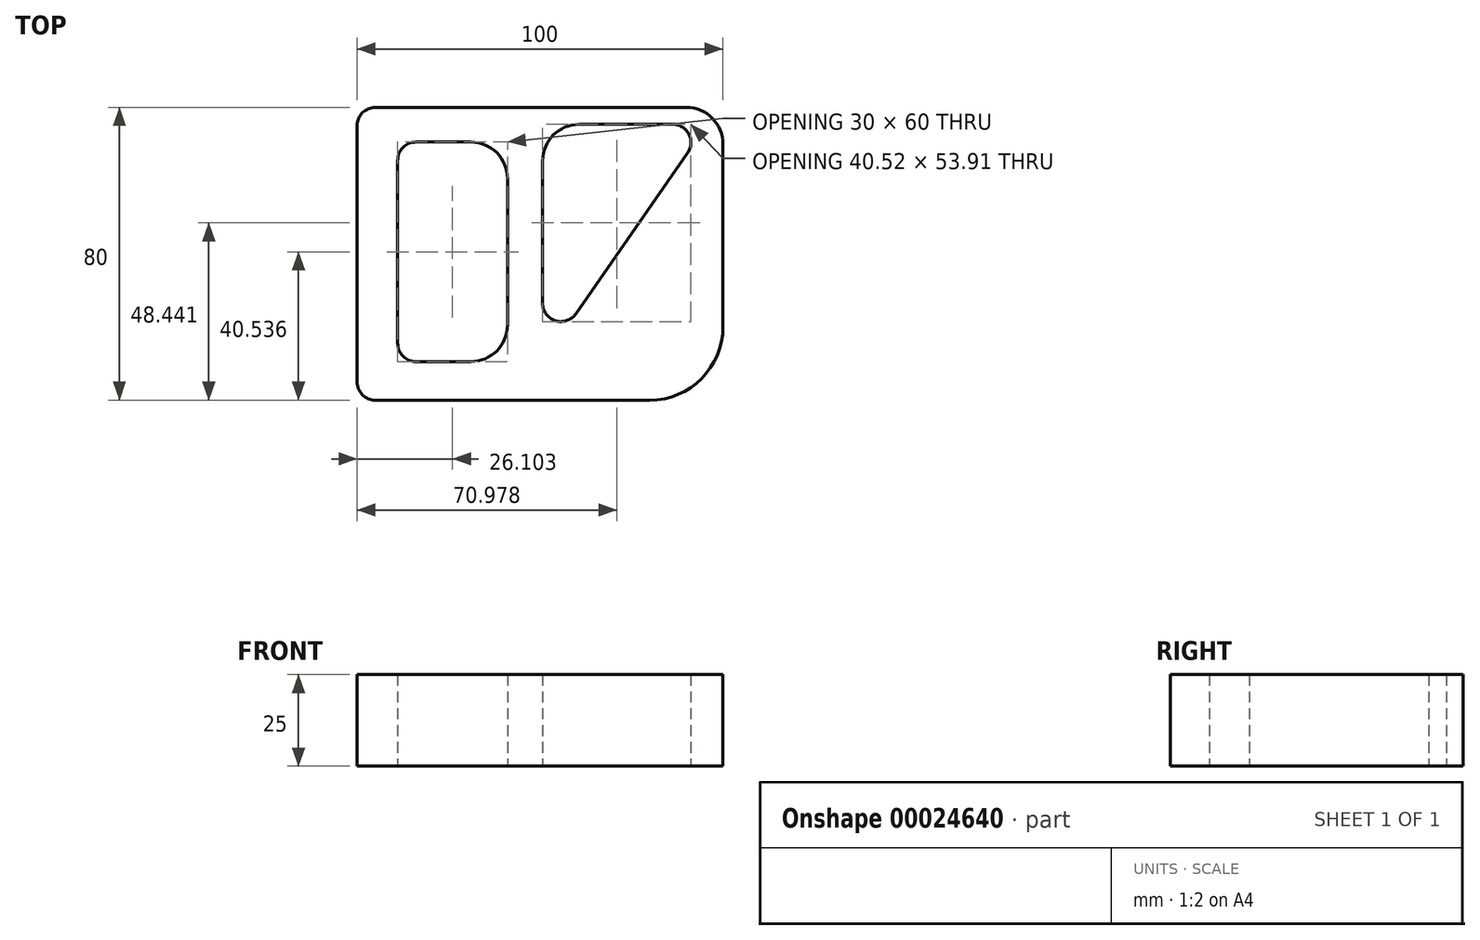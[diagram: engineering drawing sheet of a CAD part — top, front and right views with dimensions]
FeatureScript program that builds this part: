
annotation { "Feature Type Name" : "Feature", "Feature Type Description" : "" }
export const myFeature = defineFeature(function(context is Context, id is Id, definition is map)
    precondition{}
    {
        {
            var Q0;
            Q0=qCreatedBy(makeId("Top.planeOp"),FACE);
            var sketch = newSketch(context, id + "F0", { "sketchPlane" : qUnion([Q0])});
            skLineSegment(sketch, "E0.bottom", {"start": v(-40.92, 32.45) * mm, "end": v(44.08, 32.45) * mm});
            skLineSegment(sketch, "E0.top", {"start": v(-40.92, -47.55) * mm, "end": v(34.08, -47.55) * mm});
            skLineSegment(sketch, "E0.left", {"start": v(-45.92, 27.45) * mm, "end": v(-45.92, -42.55) * mm});
            skLineSegment(sketch, "E0.right", {"start": v(54.08, 22.45) * mm, "end": v(54.08, -27.55) * mm});
            skLineSegment(sketch, "E1.bottom", {"start": v(-29.82, 22.99) * mm, "end": v(-14.82, 22.99) * mm});
            skLineSegment(sketch, "E1.top", {"start": v(-29.82, -37.01) * mm, "end": v(-14.82, -37.01) * mm});
            skLineSegment(sketch, "E1.left", {"start": v(-34.82, 17.99) * mm, "end": v(-34.82, -32.01) * mm});
            skLineSegment(sketch, "E1.right", {"start": v(-4.82, 12.99) * mm, "end": v(-4.82, -27.01) * mm});
            skLineSegment(sketch, "E2", {"start": v(14.8, 27.84) * mm, "end": v(40.33, 27.84) * mm});
            skLineSegment(sketch, "E3", {"start": v(44.43, 20) * mm, "end": v(13.9, -23.92) * mm});
            skLineSegment(sketch, "E4", {"start": v(4.8, -21.06) * mm, "end": v(4.8, 17.84) * mm});
            skPoint(sketch, "E5.visualSharp", {"position": v(-45.92, 32.45) * mm});
            skArc(sketch, "E5.filletArc", {"start": v(-40.92, 32.45) * mm, "mid": v(-44.46, 30.98) * mm, "end": v(-45.92, 27.45) * mm});
            skPoint(sketch, "E6.visualSharp", {"position": v(-34.82, 22.99) * mm});
            skArc(sketch, "E6.filletArc", {"start": v(-29.82, 22.99) * mm, "mid": v(-33.35, 21.52) * mm, "end": v(-34.82, 17.99) * mm});
            skPoint(sketch, "E7.visualSharp", {"position": v(-4.82, 22.99) * mm});
            skArc(sketch, "E7.filletArc", {"start": v(-4.82, 12.99) * mm, "mid": v(-7.75, 20.06) * mm, "end": v(-14.82, 22.99) * mm});
            skPoint(sketch, "E8.visualSharp", {"position": v(-4.82, -37.01) * mm});
            skArc(sketch, "E8.filletArc", {"start": v(-14.82, -37.01) * mm, "mid": v(-7.75, -34.08) * mm, "end": v(-4.82, -27.01) * mm});
            skPoint(sketch, "E9.visualSharp", {"position": v(-34.82, -37.01) * mm});
            skArc(sketch, "E9.filletArc", {"start": v(-34.82, -32.01) * mm, "mid": v(-33.35, -35.55) * mm, "end": v(-29.82, -37.01) * mm});
            skPoint(sketch, "E10.visualSharp", {"position": v(4.8, -37.01) * mm});
            skArc(sketch, "E10.filletArc", {"start": v(4.8, -21.06) * mm, "mid": v(8.3, -25.83) * mm, "end": v(13.9, -23.92) * mm});
            skPoint(sketch, "E11.visualSharp", {"position": v(4.8, 27.84) * mm});
            skArc(sketch, "E11.filletArc", {"start": v(14.8, 27.84) * mm, "mid": v(7.73, 24.92) * mm, "end": v(4.8, 17.84) * mm});
            skArc(sketch, "E12.filletArc", {"start": v(44.43, 20) * mm, "mid": v(44.76, 25.16) * mm, "end": v(40.33, 27.84) * mm});
            skPoint(sketch, "E13.visualSharp", {"position": v(54.08, 32.45) * mm});
            skArc(sketch, "E13.filletArc", {"start": v(54.08, 22.45) * mm, "mid": v(51.15, 29.52) * mm, "end": v(44.08, 32.45) * mm});
            skPoint(sketch, "E14.visualSharp", {"position": v(-45.92, -47.55) * mm});
            skArc(sketch, "E14.filletArc", {"start": v(-45.92, -42.55) * mm, "mid": v(-44.46, -46.09) * mm, "end": v(-40.92, -47.55) * mm});
            skPoint(sketch, "E15.visualSharp", {"position": v(54.08, -47.55) * mm});
            skArc(sketch, "E15.filletArc", {"start": v(34.08, -47.55) * mm, "mid": v(48.22, -41.7) * mm, "end": v(54.08, -27.55) * mm});
            skSolve(sketch);
        }
        {
            var Q0;
            Q0 = qSketchRegion(id + "F0", true);
            extrude(context, id + "F1", {"entities" : qUnion([Q0]), "depth" : 25 * mm});
        }
    });
